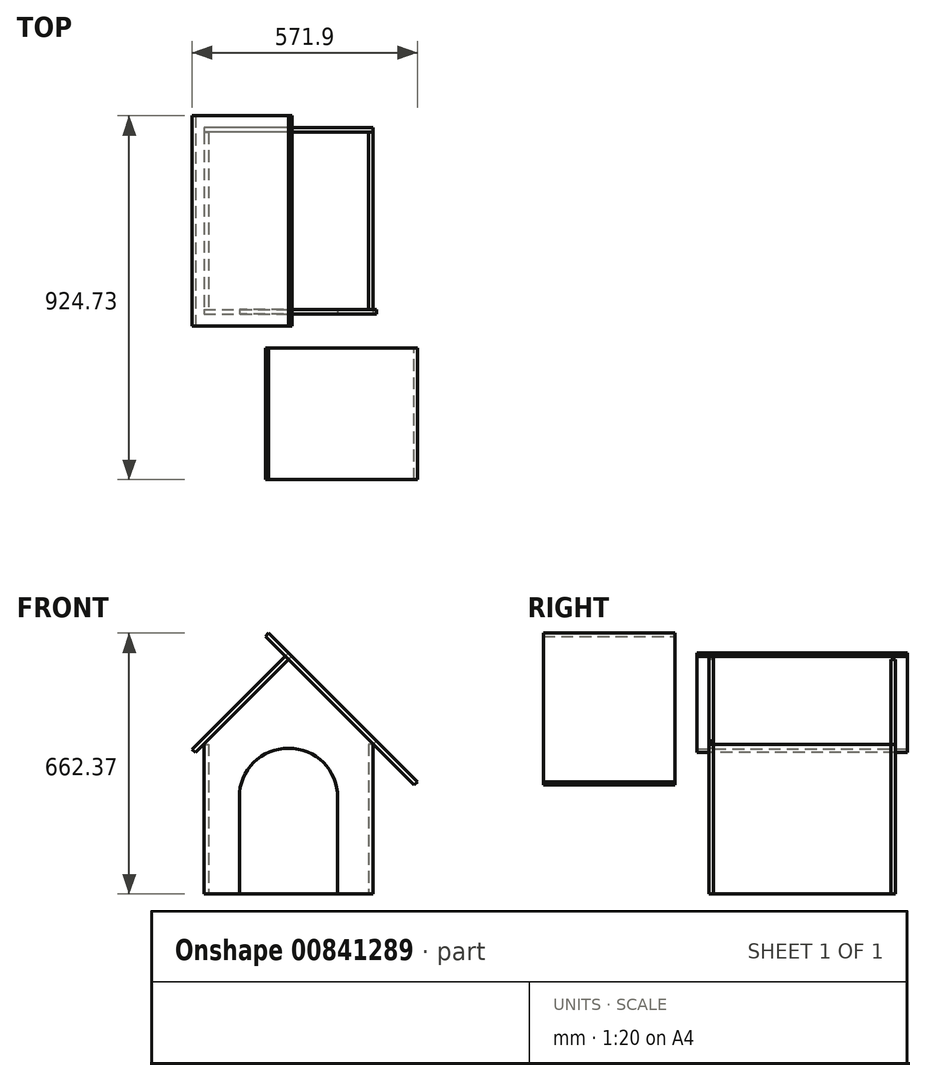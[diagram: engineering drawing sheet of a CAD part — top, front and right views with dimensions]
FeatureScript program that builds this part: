
annotation { "Feature Type Name" : "Feature", "Feature Type Description" : "" }
export const myFeature = defineFeature(function(context is Context, id is Id, definition is map)
    precondition{}
    {
        {
            var Q0;
            Q0=qCreatedBy(makeId("Front.planeOp"),FACE);
            var sketch = newSketch(context, id + "F0", { "sketchPlane" : qUnion([Q0])});
            skLineSegment(sketch, "E0.bottom", {"start": v(-215, 0) * mm, "end": v(-125, 0) * mm});
            skLineSegment(sketch, "E0.left", {"start": v(-215, 0) * mm, "end": v(-215, 380) * mm});
            skLineSegment(sketch, "E0.right", {"start": v(215, 0) * mm, "end": v(215, 380) * mm});
            skLineSegment(sketch, "E1.left", {"start": v(-125, 0) * mm, "end": v(-125, 245) * mm});
            skLineSegment(sketch, "E1.right", {"start": v(125, 0) * mm, "end": v(125, 245) * mm});
            skArc(sketch, "E2", {"start": v(125, 245) * mm, "mid": v(0, 370) * mm, "end": v(-125, 245) * mm});
            skPoint(sketch, "E3", {"position": v(0, 450) * mm});
            skLineSegment(sketch, "E4", {"start": v(-215, 380) * mm, "end": v(0, 595) * mm});
            skLineSegment(sketch, "E5", {"start": v(0, 595) * mm, "end": v(215, 380) * mm});
            skLineSegment(sketch, "E6.trimOffspring", {"start": v(125, 0) * mm, "end": v(215, 0) * mm});
            skSolve(sketch);
        }
        {
            var Q0;
            Q0 = qSketchRegion(id + "F0", true);
            extrude(context, id + "F1", {"entities" : qUnion([Q0]), "oppositeDirection" : true, "depth" : 12 * mm, "offsetDistance" : 25 * mm});
        }
        {
            var Q0;
            Q0=makeQuery(id+"F1.opExtrude","CAP_FACE",FACE,{"disambiguationData":[OSD([sQuery(id+"F0.wireOp",EDGE,"E0.bottom"),sQuery(id+"F0.wireOp",EDGE,"E0.left"),sQuery(id+"F0.wireOp",EDGE,"E0.right"),sQuery(id+"F0.wireOp",EDGE,"E1.left"),sQuery(id+"F0.wireOp",EDGE,"E1.right"),sQuery(id+"F0.wireOp",EDGE,"E2"),sQuery(id+"F0.wireOp",EDGE,"E4"),sQuery(id+"F0.wireOp",EDGE,"E5"),sQuery(id+"F0.wireOp",EDGE,"E6.trimOffspring")])],"isStart":false});
            var sketch = newSketch(context, id + "F2", { "sketchPlane" : qUnion([Q0])});
            skLineSegment(sketch, "E7.bottom", {"start": v(-215, 380) * mm, "end": v(-203, 380) * mm});
            skLineSegment(sketch, "E7.top", {"start": v(-215, 0) * mm, "end": v(-203, 0) * mm});
            skLineSegment(sketch, "E7.left", {"start": v(-215, 380) * mm, "end": v(-215, 0) * mm});
            skLineSegment(sketch, "E7.right", {"start": v(-203, 380) * mm, "end": v(-203, 0) * mm});
            skLineSegment(sketch, "E8.bottom", {"start": v(215, 380) * mm, "end": v(203, 380) * mm});
            skLineSegment(sketch, "E8.top", {"start": v(215, 0) * mm, "end": v(203, 0) * mm});
            skLineSegment(sketch, "E8.left", {"start": v(215, 380) * mm, "end": v(215, 0) * mm});
            skLineSegment(sketch, "E8.right", {"start": v(203, 380) * mm, "end": v(203, 0) * mm});
            skSolve(sketch);
        }
        {
            var Q0;
            Q0 = qSketchRegion(id + "F2", true);
            extrude(context, id + "F3", {"entities" : qUnion([Q0]), "depth" : 450 * mm, "offsetDistance" : 25 * mm});
        }
        {
            var Q0;
            Q0=makeQuery(id+"F3.opExtrude","CAP_FACE",FACE,{"disambiguationData":[OSD([sQuery(id+"F2.wireOp",EDGE,"E7.bottom"),sQuery(id+"F2.wireOp",EDGE,"E7.top"),sQuery(id+"F2.wireOp",EDGE,"E7.left"),sQuery(id+"F2.wireOp",EDGE,"E7.right")])],"isStart":false});
            var sketch = newSketch(context, id + "F4", { "sketchPlane" : qUnion([Q0])});
            skLineSegment(sketch, "E9.bottom", {"start": v(-215, 0) * mm, "end": v(60.76, 0) * mm});
            skLineSegment(sketch, "E9.left", {"start": v(-215, 0) * mm, "end": v(-215, 380) * mm});
            skLineSegment(sketch, "E9.right", {"start": v(215, 0) * mm, "end": v(215, 380) * mm});
            skPoint(sketch, "E10", {"position": v(-635.58, 561.23) * mm});
            skLineSegment(sketch, "E11", {"start": v(-215, 380) * mm, "end": v(0, 595) * mm});
            skLineSegment(sketch, "E12", {"start": v(0, 595) * mm, "end": v(215, 380) * mm});
            skLineSegment(sketch, "E13.trimOffspring", {"start": v(60.76, 0) * mm, "end": v(215, 0) * mm});
            skSolve(sketch);
        }
        {
            var Q0;
            Q0 = qSketchRegion(id + "F4", true);
            extrude(context, id + "F5", {"entities" : qUnion([Q0]), "depth" : 12 * mm, "offsetDistance" : 25 * mm});
        }
        {
            var Q0;
            Q0=makeQuery(id+"F1.opExtrude","SWEPT_FACE",FACE,{"disambiguationData":[OSD([sQuery(id+"F0.wireOp",EDGE,"E5")])]});
            var sketch = newSketch(context, id + "F6", { "sketchPlane" : qUnion([Q0])});
            skLineSegment(sketch, "E14.bottom", {"start": v(-420.73, -30) * mm, "end": v(-86.67, -30) * mm});
            skLineSegment(sketch, "E14.top", {"start": v(-420.73, 504) * mm, "end": v(-86.67, 504) * mm});
            skLineSegment(sketch, "E14.left", {"start": v(-420.73, -30) * mm, "end": v(-420.73, 504) * mm});
            skLineSegment(sketch, "E14.right", {"start": v(-86.67, -30) * mm, "end": v(-86.67, 504) * mm});
            skSolve(sketch);
        }
        {
            var Q0;
            {var subQ1=sQuery(id+"F0.wireOp",EDGE,"E5");var subQ2=makeQuery(id+"F1.opExtrude","CAP_EDGE",EDGE,{"disambiguationData":[OSD([subQ1])],"isStart":true});Q0=makeQuery(id+"F6.imprint","IMPRINT",FACE,{"disambiguationData":[TD([[makeQuery(id+"F6.imprint","IMPRINT",EDGE,{"derivedFrom":subQ2}),1.0]])]});}
            var Q1;
            {var subQ5=sQuery(id+"F6.wireOp",EDGE,"E14.bottom");Q1=makeQuery(id+"F6.imprint","IMPRINT",FACE,{"disambiguationData":[TD([[makeQuery(id+"F6.imprint","IMPRINT",EDGE,{"derivedFrom":subQ5}),1.0]])]});}
            extrude(context, id + "F7", {"entities" : qUnion([Q0, Q1]), "depth" : 12 * mm, "offsetDistance" : 25 * mm});
        }
        {
            var Q0;
            Q0=makeQuery(id+"F1.opExtrude","SWEPT_FACE",FACE,{"disambiguationData":[OSD([sQuery(id+"F0.wireOp",EDGE,"E4")])]});
            var sketch = newSketch(context, id + "F8", { "sketchPlane" : qUnion([Q0])});
            skLineSegment(sketch, "E15.bottom", {"start": v(-504, 86.67) * mm, "end": v(30, 86.67) * mm});
            skLineSegment(sketch, "E15.top", {"start": v(-504, 432.73) * mm, "end": v(30, 432.73) * mm});
            skLineSegment(sketch, "E15.left", {"start": v(-504, 86.67) * mm, "end": v(-504, 432.73) * mm});
            skLineSegment(sketch, "E15.right", {"start": v(30, 86.67) * mm, "end": v(30, 432.73) * mm});
            skSolve(sketch);
        }
        {
            var Q0;
            Q0 = qSketchRegion(id + "F8", true);
            extrude(context, id + "F9", {"entities" : qUnion([Q0]), "depth" : 12 * mm, "offsetDistance" : 25 * mm});
        }
    });
